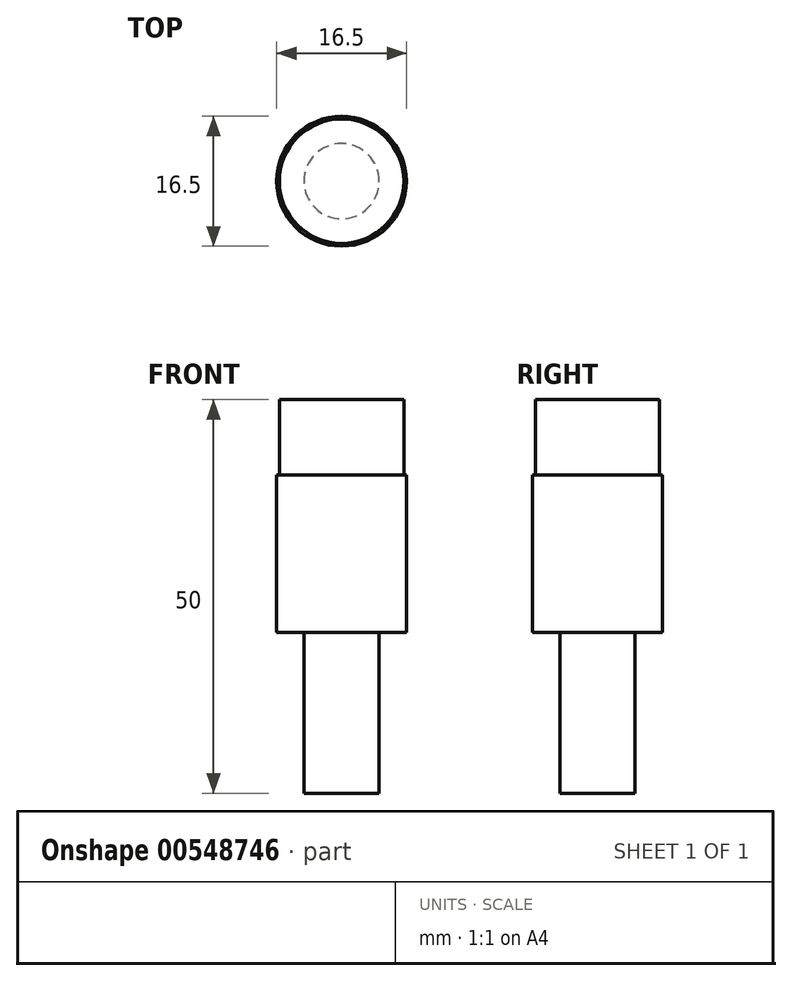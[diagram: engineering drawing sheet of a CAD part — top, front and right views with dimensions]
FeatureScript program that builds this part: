
annotation { "Feature Type Name" : "Feature", "Feature Type Description" : "" }
export const myFeature = defineFeature(function(context is Context, id is Id, definition is map)
    precondition{}
    {
        {
            var Q0;
            Q0=qCreatedBy(makeId("Top.planeOp"),FACE);
            var sketch = newSketch(context, id + "F0", { "sketchPlane" : qUnion([Q0])});
            skCircle(sketch, "E0", {"center": v(0, 0) * mm, "radius": 8.25 * mm});
            skSolve(sketch);
        }
        {
            var Q0;
            Q0=qSketchRegion(id+"F0",true);
            extrude(context, id + "F1", {"entities" : qUnion([Q0]), "depth" : 20 * mm, "offsetDistance" : 25.4 * mm});
        }
        {
            var Q0;
            Q0=makeQuery(id+"F1.opExtrude","CAP_FACE",FACE,{"disambiguationData":[OSD([sQuery(id+"F0.wireOp",EDGE,"E0")])],"isStart":false});
            var sketch = newSketch(context, id + "F2", { "sketchPlane" : qUnion([Q0])});
            skCircle(sketch, "E1", {"center": v(0, 0) * mm, "radius": 7.9 * mm});
            skSolve(sketch);
        }
        {
            var Q0;
            Q0=qSketchRegion(id+"F2",true);
            extrude(context, id + "F3", {"entities" : qUnion([Q0]), "operationType" : NewBodyOperationType.ADD, "depth" : 9.6 * mm, "offsetDistance" : 25.4 * mm});
        }
        {
            var Q0;
            Q0=makeQuery(id+"F1.opExtrude","CAP_FACE",FACE,{"disambiguationData":[OSD([sQuery(id+"F0.wireOp",EDGE,"E0")])],"isStart":true});
            var sketch = newSketch(context, id + "F4", { "sketchPlane" : qUnion([Q0])});
            skCircle(sketch, "E2", {"center": v(0, 0) * mm, "radius": 4.78 * mm});
            skSolve(sketch);
        }
        {
            var Q0;
            Q0=qSketchRegion(id+"F4",true);
            extrude(context, id + "F5", {"entities" : qUnion([Q0]), "operationType" : NewBodyOperationType.ADD, "depth" : 20.4 * mm, "offsetDistance" : 25 * mm});
        }
    });
